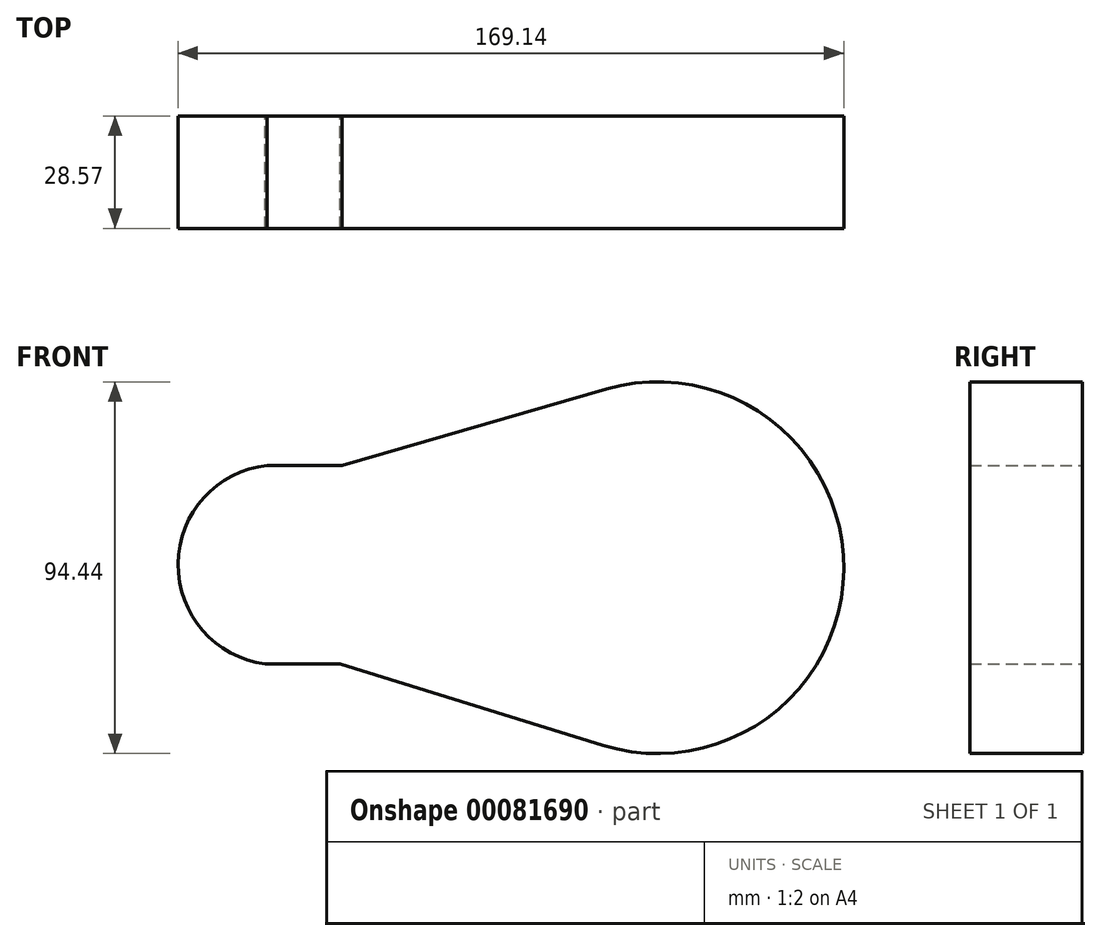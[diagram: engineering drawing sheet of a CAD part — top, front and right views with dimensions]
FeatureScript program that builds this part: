
annotation { "Feature Type Name" : "Feature", "Feature Type Description" : "" }
export const myFeature = defineFeature(function(context is Context, id is Id, definition is map)
    precondition{}
    {
        {
            var Q0;
            Q0=qCreatedBy(makeId("Front.planeOp"),FACE);
            var sketch = newSketch(context, id + "F0", { "sketchPlane" : qUnion([Q0])});
            skArc(sketch, "E0", {"start": v(-13.97, -45.1) * mm, "mid": v(47.22, -0.46) * mm, "end": v(-13.1, 45.37) * mm});
            skArc(sketch, "E1", {"start": v(-93.8, 26) * mm, "mid": v(-121.92, 0.5) * mm, "end": v(-93.3, -24.45) * mm});
            skLineSegment(sketch, "E2", {"start": v(-99.25, 26) * mm, "end": v(-80.2, 26) * mm});
            skLineSegment(sketch, "E3", {"start": v(-99.74, -24.45) * mm, "end": v(-80.7, -24.45) * mm});
            skLineSegment(sketch, "E4", {"start": v(-80.2, 26) * mm, "end": v(-13.1, 45.37) * mm});
            skLineSegment(sketch, "E5", {"start": v(-80.7, -24.45) * mm, "end": v(-13.97, -45.1) * mm});
            skSolve(sketch);
        }
        {
            var Q0;
            Q0=makeQuery(id+"F0.imprint","IMPRINT",FACE,{"disambiguationData":[TD([[makeQuery(id+"F0.imprint","IMPRINT",EDGE,{"derivedFrom":sQuery(id+"F0.wireOp",EDGE,"E0")}),1.0]])]});
            extrude(context, id + "F1", {"entities" : qUnion([Q0]), "depth" : 28.57 * mm});
        }
    });
